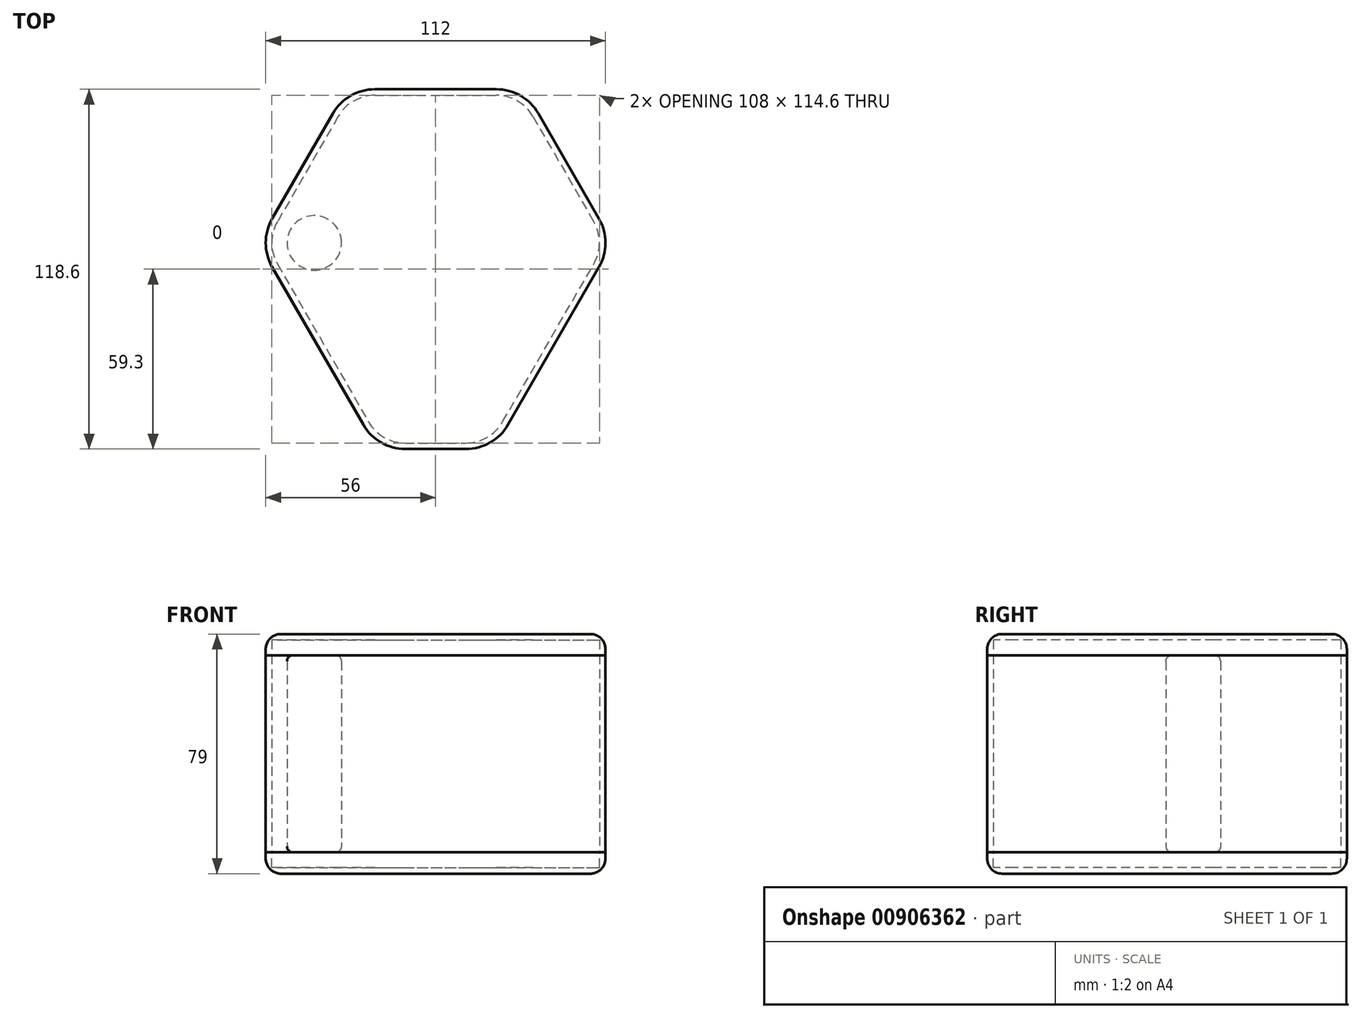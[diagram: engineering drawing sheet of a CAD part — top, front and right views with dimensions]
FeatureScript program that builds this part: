
annotation { "Feature Type Name" : "Feature", "Feature Type Description" : "" }
export const myFeature = defineFeature(function(context is Context, id is Id, definition is map)
    precondition{}
    {
        {
            var Q0;
            Q0=qCreatedBy(makeId("Top.planeOp"),FACE);
            var sketch = newSketch(context, id + "F0", { "sketchPlane" : qUnion([Q0])});
            skCircle(sketch, "E0", {"center": v(0, 0) * mm, "radius": 9 * mm});
            skCircle(sketch, "E1.1.0.0", {"center": v(20, 0) * mm, "radius": 9 * mm});
            skCircle(sketch, "E1.3.0.0", {"center": v(60, 0) * mm, "radius": 9 * mm});
            skLineSegment(sketch, "E1.direction1", {"start": v(0, 0) * mm, "end": v(20, 0) * mm, "construction": true});
            skLineSegment(sketch, "E1.direction2", {"start": v(0, 0) * mm, "end": v(10.41, 17.55) * mm, "construction": true});
            skCircle(sketch, "E2", {"center": v(10, 17.32) * mm, "radius": 9 * mm});
            skCircle(sketch, "E3.1.0.0", {"center": v(30, 17.32) * mm, "radius": 9 * mm});
            skCircle(sketch, "E3.2.0.0", {"center": v(50, 17.32) * mm, "radius": 9 * mm});
            skLineSegment(sketch, "E3.direction1", {"start": v(10, 17.32) * mm, "end": v(30, 17.32) * mm, "construction": true});
            skCircle(sketch, "E4", {"center": v(20, 34.64) * mm, "radius": 9 * mm});
            skCircle(sketch, "E5.1.0.0", {"center": v(40, 34.64) * mm, "radius": 9 * mm});
            skLineSegment(sketch, "E5.direction1", {"start": v(20, 34.64) * mm, "end": v(40, 34.64) * mm, "construction": true});
            skCircle(sketch, "E6.MirrorC", {"center": v(20, -34.64) * mm, "radius": 9 * mm});
            skCircle(sketch, "E7.MirrorC", {"center": v(40, -34.64) * mm, "radius": 9 * mm});
            skCircle(sketch, "E8.MirrorC", {"center": v(30, -17.32) * mm, "radius": 9 * mm});
            skCircle(sketch, "E9.MirrorC", {"center": v(10, -17.32) * mm, "radius": 9 * mm});
            skCircle(sketch, "E10.MirrorC", {"center": v(50, -17.32) * mm, "radius": 9 * mm});
            skCircle(sketch, "E11.1.0.0", {"center": v(60, 34.64) * mm, "radius": 9 * mm});
            skCircle(sketch, "E11.1.0.1", {"center": v(70, 17.32) * mm, "radius": 9 * mm});
            skCircle(sketch, "E11.1.0.2", {"center": v(80, 0) * mm, "radius": 9 * mm});
            skCircle(sketch, "E11.1.0.3", {"center": v(70, -17.32) * mm, "radius": 9 * mm});
            skCircle(sketch, "E11.1.0.4", {"center": v(60, -34.64) * mm, "radius": 9 * mm});
            skLineSegment(sketch, "E11.direction1", {"start": v(40, -34.64) * mm, "end": v(60, -34.64) * mm, "construction": true});
            skCircle(sketch, "E12", {"center": v(30, -51.96) * mm, "radius": 9 * mm});
            skCircle(sketch, "E13", {"center": v(50, -51.96) * mm, "radius": 9 * mm});
            skSolve(sketch);
        }
        {
            var Q0;
            Q0=makeQuery(id+"F0.imprint","IMPRINT",FACE,{"disambiguationData":[TD([[makeQuery(id+"F0.imprint","IMPRINT",EDGE,{"derivedFrom":sQuery(id+"F0.wireOp",EDGE,"E0")}),1.0]])]});
            extrude(context, id + "F1", {"entities" : qUnion([Q0]), "depth" : 65 * mm, "offsetDistance" : 25 * mm});
        }
        {
            var Q0;
            Q0=makeQuery(id+"F1.opExtrude","CAP_FACE",FACE,{"disambiguationData":[OSD([sQuery(id+"F0.wireOp",EDGE,"E0")])],"isStart":false});
            var Q1;
            Q1=makeQuery(id+"F1.opExtrude","CAP_FACE",FACE,{"disambiguationData":[OSD([sQuery(id+"F0.wireOp",EDGE,"E0")])],"isStart":true});
            fillet(context, id + "F2", {"entities" : qUnion([Q0, Q1]), "radius" : 2 * mm, "tangentPropagation" : true, "allowEdgeOverflow" : false});
        }
        {
            var Q0;
            Q0=qCreatedBy(makeId("Top.planeOp"),FACE);
            var sketch = newSketch(context, id + "F3", { "sketchPlane" : qUnion([Q0])});
            skArc(sketch, "E14.0", {"start": v(20, 43.64) * mm, "mid": v(15.5, 42.44) * mm, "end": v(12.2, 39.14) * mm});
            skArc(sketch, "E15.0", {"start": v(-7.8, 4.5) * mm, "mid": v(-9, 0) * mm, "end": v(-7.8, -4.5) * mm});
            skArc(sketch, "E16.0", {"start": v(22.2, -56.46) * mm, "mid": v(25.5, -59.76) * mm, "end": v(30, -60.96) * mm});
            skArc(sketch, "E17.0", {"start": v(50, -60.96) * mm, "mid": v(54.5, -59.76) * mm, "end": v(57.8, -56.46) * mm});
            skArc(sketch, "E18.0", {"start": v(87.8, -4.5) * mm, "mid": v(89, 0) * mm, "end": v(87.8, 4.5) * mm});
            skArc(sketch, "E19.0", {"start": v(67.8, 39.14) * mm, "mid": v(64.5, 42.44) * mm, "end": v(60, 43.64) * mm});
            skLineSegment(sketch, "E20", {"start": v(12.2, 39.14) * mm, "end": v(-7.8, 4.5) * mm});
            skLineSegment(sketch, "E21", {"start": v(-7.8, -4.5) * mm, "end": v(22.2, -56.46) * mm});
            skLineSegment(sketch, "E22", {"start": v(30, -60.96) * mm, "end": v(50, -60.96) * mm});
            skLineSegment(sketch, "E23", {"start": v(20, 43.64) * mm, "end": v(60, 43.64) * mm});
            skLineSegment(sketch, "E24", {"start": v(67.8, 39.14) * mm, "end": v(87.8, 4.5) * mm});
            skLineSegment(sketch, "E25", {"start": v(57.8, -56.46) * mm, "end": v(87.8, -4.5) * mm});
            skArc(sketch, "E26.0", {"start": v(20, 48.64) * mm, "mid": v(13, 46.77) * mm, "end": v(7.88, 41.64) * mm});
            skLineSegment(sketch, "E26.1", {"start": v(30, -65.96) * mm, "end": v(50, -65.96) * mm});
            skArc(sketch, "E26.2", {"start": v(17.88, -58.96) * mm, "mid": v(23, -64.09) * mm, "end": v(30, -65.96) * mm});
            skLineSegment(sketch, "E26.3", {"start": v(-12.12, -7) * mm, "end": v(17.88, -58.96) * mm});
            skArc(sketch, "E26.4", {"start": v(-12.12, 7) * mm, "mid": v(-14, 0) * mm, "end": v(-12.12, -7) * mm});
            skArc(sketch, "E26.5", {"start": v(50, -65.96) * mm, "mid": v(57, -64.09) * mm, "end": v(62.12, -58.96) * mm});
            skLineSegment(sketch, "E26.6", {"start": v(7.88, 41.64) * mm, "end": v(-12.12, 7) * mm});
            skLineSegment(sketch, "E26.7", {"start": v(62.12, -58.96) * mm, "end": v(92.12, -7) * mm});
            skArc(sketch, "E26.8", {"start": v(92.12, -7) * mm, "mid": v(94, 0) * mm, "end": v(92.12, 7) * mm});
            skLineSegment(sketch, "E26.9", {"start": v(72.12, 41.64) * mm, "end": v(92.12, 7) * mm});
            skArc(sketch, "E26.10", {"start": v(72.12, 41.64) * mm, "mid": v(67, 46.77) * mm, "end": v(60, 48.64) * mm});
            skLineSegment(sketch, "E26.11", {"start": v(20, 48.64) * mm, "end": v(60, 48.64) * mm});
            skArc(sketch, "E27.0", {"start": v(20, 50.64) * mm, "mid": v(12, 48.5) * mm, "end": v(6.14, 42.64) * mm});
            skLineSegment(sketch, "E27.1", {"start": v(30, -67.96) * mm, "end": v(50, -67.96) * mm});
            skArc(sketch, "E27.2", {"start": v(16.14, -59.96) * mm, "mid": v(22, -65.82) * mm, "end": v(30, -67.96) * mm});
            skLineSegment(sketch, "E27.3", {"start": v(-13.86, -8) * mm, "end": v(16.14, -59.96) * mm});
            skArc(sketch, "E27.4", {"start": v(-13.86, 8) * mm, "mid": v(-16, 0) * mm, "end": v(-13.86, -8) * mm});
            skArc(sketch, "E27.5", {"start": v(50, -67.96) * mm, "mid": v(58, -65.82) * mm, "end": v(63.86, -59.96) * mm});
            skLineSegment(sketch, "E27.6", {"start": v(6.14, 42.64) * mm, "end": v(-13.86, 8) * mm});
            skLineSegment(sketch, "E27.7", {"start": v(63.86, -59.96) * mm, "end": v(93.86, -8) * mm});
            skArc(sketch, "E27.8", {"start": v(93.86, -8) * mm, "mid": v(96, 0) * mm, "end": v(93.86, 8) * mm});
            skLineSegment(sketch, "E27.9", {"start": v(73.86, 42.64) * mm, "end": v(93.86, 8) * mm});
            skArc(sketch, "E27.10", {"start": v(73.86, 42.64) * mm, "mid": v(68, 48.5) * mm, "end": v(60, 50.64) * mm});
            skLineSegment(sketch, "E27.11", {"start": v(20, 50.64) * mm, "end": v(60, 50.64) * mm});
            skSolve(sketch);
        }
        {
            var Q0;
            Q0=makeQuery(id+"F3.imprint","IMPRINT",FACE,{"disambiguationData":[TD([[makeQuery(id+"F3.imprint","IMPRINT",EDGE,{"derivedFrom":sQuery(id+"F3.wireOp",EDGE,"E26.0")}),-1.0]])]});
            extrude(context, id + "F4", {"entities" : qUnion([Q0]), "depth" : 65 * mm, "offsetDistance" : 25 * mm});
        }
        {
            var Q0;
            Q0=makeQuery(id+"F4.opExtrude","CAP_FACE",FACE,{"disambiguationData":[OSD([sQuery(id+"F3.wireOp",EDGE,"E26.0"),sQuery(id+"F3.wireOp",EDGE,"E26.1"),sQuery(id+"F3.wireOp",EDGE,"E26.2"),sQuery(id+"F3.wireOp",EDGE,"E26.3"),sQuery(id+"F3.wireOp",EDGE,"E26.4"),sQuery(id+"F3.wireOp",EDGE,"E26.5"),sQuery(id+"F3.wireOp",EDGE,"E26.6"),sQuery(id+"F3.wireOp",EDGE,"E26.7"),sQuery(id+"F3.wireOp",EDGE,"E26.8"),sQuery(id+"F3.wireOp",EDGE,"E26.9"),sQuery(id+"F3.wireOp",EDGE,"E26.10"),sQuery(id+"F3.wireOp",EDGE,"E26.11"),sQuery(id+"F3.wireOp",EDGE,"E27.0"),sQuery(id+"F3.wireOp",EDGE,"E27.1"),sQuery(id+"F3.wireOp",EDGE,"E27.2"),sQuery(id+"F3.wireOp",EDGE,"E27.3"),sQuery(id+"F3.wireOp",EDGE,"E27.4"),sQuery(id+"F3.wireOp",EDGE,"E27.5"),sQuery(id+"F3.wireOp",EDGE,"E27.6"),sQuery(id+"F3.wireOp",EDGE,"E27.7"),sQuery(id+"F3.wireOp",EDGE,"E27.8"),sQuery(id+"F3.wireOp",EDGE,"E27.9"),sQuery(id+"F3.wireOp",EDGE,"E27.10"),sQuery(id+"F3.wireOp",EDGE,"E27.11")])],"isStart":false});
            var sketch = newSketch(context, id + "F5", { "sketchPlane" : qUnion([Q0])});
            skArc(sketch, "E28.0.0", {"start": v(50, -67.96) * mm, "mid": v(58, -65.82) * mm, "end": v(63.86, -59.96) * mm});
            skLineSegment(sketch, "E28.0.1", {"start": v(63.86, -59.96) * mm, "end": v(93.86, -8) * mm});
            skArc(sketch, "E28.0.2", {"start": v(93.86, -8) * mm, "mid": v(96, 0) * mm, "end": v(93.86, 8) * mm});
            skLineSegment(sketch, "E28.0.3", {"start": v(93.86, 8) * mm, "end": v(73.86, 42.64) * mm});
            skArc(sketch, "E28.0.4", {"start": v(73.86, 42.64) * mm, "mid": v(68, 48.5) * mm, "end": v(60, 50.64) * mm});
            skLineSegment(sketch, "E28.0.5", {"start": v(60, 50.64) * mm, "end": v(20, 50.64) * mm});
            skArc(sketch, "E28.0.6", {"start": v(20, 50.64) * mm, "mid": v(12, 48.5) * mm, "end": v(6.14, 42.64) * mm});
            skLineSegment(sketch, "E28.0.7", {"start": v(6.14, 42.64) * mm, "end": v(-13.86, 8) * mm});
            skArc(sketch, "E28.0.8", {"start": v(-13.86, 8) * mm, "mid": v(-16, 0) * mm, "end": v(-13.86, -8) * mm});
            skLineSegment(sketch, "E28.0.9", {"start": v(-13.86, -8) * mm, "end": v(16.14, -59.96) * mm});
            skArc(sketch, "E28.0.10", {"start": v(16.14, -59.96) * mm, "mid": v(22, -65.82) * mm, "end": v(30, -67.96) * mm});
            skLineSegment(sketch, "E28.0.11", {"start": v(30, -67.96) * mm, "end": v(50, -67.96) * mm});
            skLineSegment(sketch, "E29.0", {"start": v(7.88, 41.64) * mm, "end": v(-12.12, 7) * mm});
            skArc(sketch, "E30.0", {"start": v(-12.12, 7) * mm, "mid": v(-14, 0) * mm, "end": v(-12.12, -7) * mm});
            skArc(sketch, "E31.0", {"start": v(20, 48.64) * mm, "mid": v(13, 46.77) * mm, "end": v(7.88, 41.64) * mm});
            skLineSegment(sketch, "E32.0", {"start": v(20, 48.64) * mm, "end": v(60, 48.64) * mm});
            skArc(sketch, "E33.0", {"start": v(72.12, 41.64) * mm, "mid": v(67, 46.77) * mm, "end": v(60, 48.64) * mm});
            skLineSegment(sketch, "E34.0", {"start": v(72.12, 41.64) * mm, "end": v(92.12, 7) * mm});
            skArc(sketch, "E35.0", {"start": v(92.12, -7) * mm, "mid": v(94, 0) * mm, "end": v(92.12, 7) * mm});
            skLineSegment(sketch, "E36.0", {"start": v(62.12, -58.96) * mm, "end": v(92.12, -7) * mm});
            skArc(sketch, "E37.0", {"start": v(50, -65.96) * mm, "mid": v(57, -64.09) * mm, "end": v(62.12, -58.96) * mm});
            skLineSegment(sketch, "E38.0", {"start": v(30, -65.96) * mm, "end": v(50, -65.96) * mm});
            skArc(sketch, "E39.0", {"start": v(17.88, -58.96) * mm, "mid": v(23, -64.09) * mm, "end": v(30, -65.96) * mm});
            skLineSegment(sketch, "E40.0", {"start": v(-12.12, -7) * mm, "end": v(17.88, -58.96) * mm});
            skSolve(sketch);
        }
        {
            var Q0;
            Q0=makeQuery(id+"F5.imprint","IMPRINT",FACE,{"disambiguationData":[TD([[makeQuery(id+"F5.imprint","IMPRINT",EDGE,{"derivedFrom":sQuery(id+"F5.wireOp",EDGE,"E28.0.0")}),1.0]])]});
            extrude(context, id + "F6", {"entities" : qUnion([Q0]), "depth" : 5 * mm, "offsetDistance" : 25 * mm});
        }
        {
            var Q0;
            Q0=makeQuery(id+"F6.opExtrude","CAP_FACE",FACE,{"disambiguationData":[OSD([sQuery(id+"F5.wireOp",EDGE,"E28.0.0"),sQuery(id+"F5.wireOp",EDGE,"E28.0.1"),sQuery(id+"F5.wireOp",EDGE,"E28.0.2"),sQuery(id+"F5.wireOp",EDGE,"E28.0.3"),sQuery(id+"F5.wireOp",EDGE,"E28.0.4"),sQuery(id+"F5.wireOp",EDGE,"E28.0.5"),sQuery(id+"F5.wireOp",EDGE,"E28.0.6"),sQuery(id+"F5.wireOp",EDGE,"E28.0.7"),sQuery(id+"F5.wireOp",EDGE,"E28.0.8"),sQuery(id+"F5.wireOp",EDGE,"E28.0.9"),sQuery(id+"F5.wireOp",EDGE,"E28.0.10"),sQuery(id+"F5.wireOp",EDGE,"E28.0.11"),sQuery(id+"F5.wireOp",EDGE,"E29.0"),sQuery(id+"F5.wireOp",EDGE,"E30.0"),sQuery(id+"F5.wireOp",EDGE,"E31.0"),sQuery(id+"F5.wireOp",EDGE,"E32.0"),sQuery(id+"F5.wireOp",EDGE,"E33.0"),sQuery(id+"F5.wireOp",EDGE,"E34.0"),sQuery(id+"F5.wireOp",EDGE,"E35.0"),sQuery(id+"F5.wireOp",EDGE,"E36.0"),sQuery(id+"F5.wireOp",EDGE,"E37.0"),sQuery(id+"F5.wireOp",EDGE,"E38.0"),sQuery(id+"F5.wireOp",EDGE,"E39.0"),sQuery(id+"F5.wireOp",EDGE,"E40.0")])],"isStart":false});
            var sketch = newSketch(context, id + "F7", { "sketchPlane" : qUnion([Q0])});
            skLineSegment(sketch, "E41.0.0", {"start": v(30, -67.96) * mm, "end": v(50, -67.96) * mm});
            skArc(sketch, "E41.0.1", {"start": v(50, -67.96) * mm, "mid": v(58, -65.82) * mm, "end": v(63.86, -59.96) * mm});
            skLineSegment(sketch, "E41.0.2", {"start": v(63.86, -59.96) * mm, "end": v(93.86, -8) * mm});
            skArc(sketch, "E41.0.3", {"start": v(93.86, -8) * mm, "mid": v(96, 0) * mm, "end": v(93.86, 8) * mm});
            skLineSegment(sketch, "E41.0.4", {"start": v(93.86, 8) * mm, "end": v(73.86, 42.64) * mm});
            skArc(sketch, "E41.0.5", {"start": v(73.86, 42.64) * mm, "mid": v(68, 48.5) * mm, "end": v(60, 50.64) * mm});
            skLineSegment(sketch, "E41.0.6", {"start": v(60, 50.64) * mm, "end": v(20, 50.64) * mm});
            skArc(sketch, "E41.0.7", {"start": v(20, 50.64) * mm, "mid": v(12, 48.5) * mm, "end": v(6.14, 42.64) * mm});
            skLineSegment(sketch, "E41.0.8", {"start": v(6.14, 42.64) * mm, "end": v(-13.86, 8) * mm});
            skArc(sketch, "E41.0.9", {"start": v(-13.86, 8) * mm, "mid": v(-16, 0) * mm, "end": v(-13.86, -8) * mm});
            skLineSegment(sketch, "E41.0.10", {"start": v(-13.86, -8) * mm, "end": v(16.14, -59.96) * mm});
            skArc(sketch, "E41.0.11", {"start": v(16.14, -59.96) * mm, "mid": v(22, -65.82) * mm, "end": v(30, -67.96) * mm});
            skSolve(sketch);
        }
        {
            var Q0;
            Q0=makeQuery(id+"F7.imprint","IMPRINT",FACE,{"disambiguationData":[TD([[makeQuery(id+"F7.imprint","IMPRINT",EDGE,{"derivedFrom":makeQuery(id+"F6.opExtrude","CAP_EDGE",EDGE,{"disambiguationData":[OSD([sQuery(id+"F5.wireOp",EDGE,"E29.0")])],"isStart":false})}),1.0]])]});
            var Q1;
            Q1=makeQuery(id+"F7.imprint","IMPRINT",FACE,{"disambiguationData":[TD([[makeQuery(id+"F7.imprint","IMPRINT",EDGE,{"derivedFrom":sQuery(id+"F7.wireOp",EDGE,"E41.0.0")}),1.0]])]});
            extrude(context, id + "F8", {"entities" : qUnion([Q0, Q1]), "operationType" : NewBodyOperationType.ADD, "depth" : 2 * mm, "offsetDistance" : 25 * mm});
        }
        {
            var Q0;
            Q0=makeQuery(id+"F8.opExtrude","CAP_EDGE",EDGE,{"disambiguationData":[OSD([sQuery(id+"F7.wireOp",EDGE,"E41.0.8")])],"isStart":false});
            var Q1;
            Q1=makeQuery(id+"F6.opExtrude","CAP_EDGE",EDGE,{"disambiguationData":[OSD([sQuery(id+"F5.wireOp",EDGE,"E33.0")])],"isStart":false});
            fillet(context, id + "F9", {"entities" : qUnion([Q0, Q1]), "radius" : 5 * mm, "tangentPropagation" : true, "allowEdgeOverflow" : false});
        }
        {
            var Q0;
            Q0=qCreatedBy(makeId("Top.planeOp"),FACE);
            cPlane(context, id + "F10", {"entities" : qUnion([Q0]), "cplaneType" : CPlaneType.OFFSET, "offset" : 32.5 * mm, "width" : 150 * mm, "height" : 150 * mm});
        }
        {
            var Q0;
            Q0=makeQuery(id+"F6.opExtrude","SWEPT_BODY",BODY,{"disambiguationData":[OSD([sQuery(id+"F5.wireOp",EDGE,"E28.0.0"),sQuery(id+"F5.wireOp",EDGE,"E28.0.1"),sQuery(id+"F5.wireOp",EDGE,"E28.0.2"),sQuery(id+"F5.wireOp",EDGE,"E28.0.3"),sQuery(id+"F5.wireOp",EDGE,"E28.0.4"),sQuery(id+"F5.wireOp",EDGE,"E28.0.5"),sQuery(id+"F5.wireOp",EDGE,"E28.0.6"),sQuery(id+"F5.wireOp",EDGE,"E28.0.7"),sQuery(id+"F5.wireOp",EDGE,"E28.0.8"),sQuery(id+"F5.wireOp",EDGE,"E28.0.9"),sQuery(id+"F5.wireOp",EDGE,"E28.0.10"),sQuery(id+"F5.wireOp",EDGE,"E28.0.11"),sQuery(id+"F5.wireOp",EDGE,"E29.0"),sQuery(id+"F5.wireOp",EDGE,"E30.0"),sQuery(id+"F5.wireOp",EDGE,"E31.0"),sQuery(id+"F5.wireOp",EDGE,"E32.0"),sQuery(id+"F5.wireOp",EDGE,"E33.0"),sQuery(id+"F5.wireOp",EDGE,"E34.0"),sQuery(id+"F5.wireOp",EDGE,"E35.0"),sQuery(id+"F5.wireOp",EDGE,"E36.0"),sQuery(id+"F5.wireOp",EDGE,"E37.0"),sQuery(id+"F5.wireOp",EDGE,"E38.0"),sQuery(id+"F5.wireOp",EDGE,"E39.0"),sQuery(id+"F5.wireOp",EDGE,"E40.0")])]});
            var Q1;
            Q1=qCreatedBy(id+"F10.planeOp",FACE);
            mirror(context, id + "F11", {"entities" : qUnion([Q0]), "mirrorPlane" : qUnion([Q1])});
        }
    });
